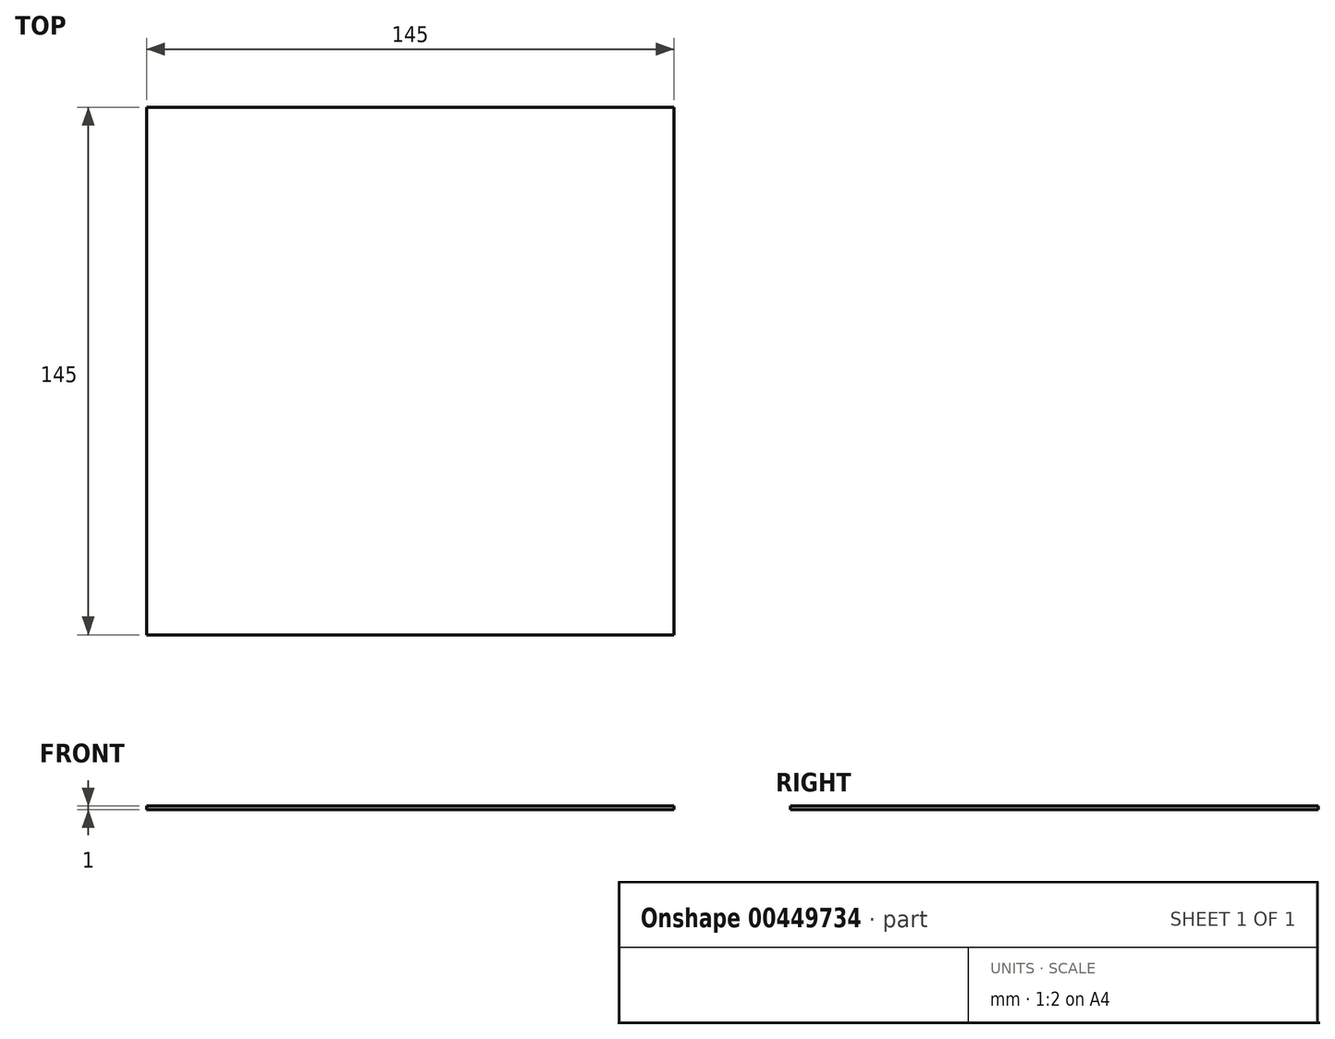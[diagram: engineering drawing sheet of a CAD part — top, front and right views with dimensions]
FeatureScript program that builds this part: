
annotation { "Feature Type Name" : "Feature", "Feature Type Description" : "" }
export const myFeature = defineFeature(function(context is Context, id is Id, definition is map)
    precondition{}
    {
        {
            var Q0;
            Q0=qCreatedBy(makeId("Top.planeOp"),FACE);
            var sketch = newSketch(context, id + "F0", { "sketchPlane" : qUnion([Q0])});
            skLineSegment(sketch, "E0.bottom", {"start": v(72.5, 72.5) * mm, "end": v(-72.5, 72.5) * mm});
            skLineSegment(sketch, "E0.top", {"start": v(72.5, -72.5) * mm, "end": v(-72.5, -72.5) * mm});
            skLineSegment(sketch, "E0.left", {"start": v(72.5, 72.5) * mm, "end": v(72.5, -72.5) * mm});
            skLineSegment(sketch, "E0.right", {"start": v(-72.5, 72.5) * mm, "end": v(-72.5, -72.5) * mm});
            skPoint(sketch, "E0.middle", {"position": v(0, 0) * mm});
            skSolve(sketch);
        }
        {
            var Q0;
            Q0 = qSketchRegion(id + "F0", true);
            extrude(context, id + "F1", {"entities" : qUnion([Q0]), "depth" : 1 * mm});
        }
    });
